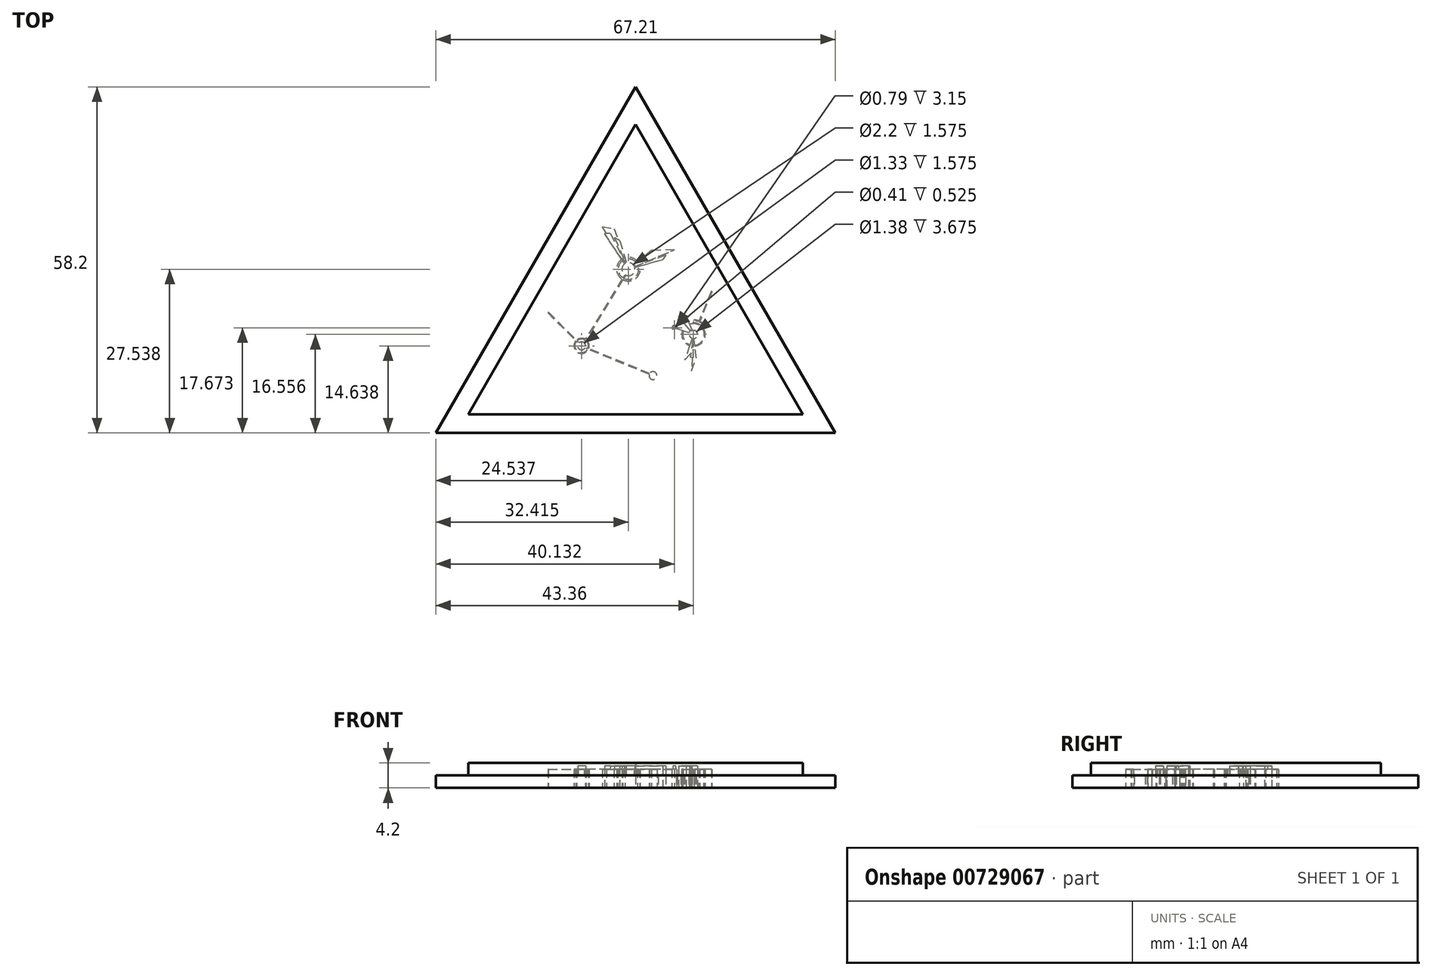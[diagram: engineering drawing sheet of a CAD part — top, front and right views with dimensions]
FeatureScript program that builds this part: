
annotation { "Feature Type Name" : "Feature", "Feature Type Description" : "" }
export const myFeature = defineFeature(function(context is Context, id is Id, definition is map)
    precondition{}
    {
        {
            var Q0;
            Q0=qCreatedBy(makeId("Top.planeOp"),FACE);
            var sketch = newSketch(context, id + "F0", { "sketchPlane" : qUnion([Q0])});
            skLineSegment(sketch, "E0", {"start": v(-5.3, -0.9) * mm, "end": v(-32.1, 45.54) * mm});
            skLineSegment(sketch, "E1", {"start": v(-58.9, -0.9) * mm, "end": v(-5.3, -0.9) * mm});
            skLineSegment(sketch, "E2", {"start": v(-58.9, -0.9) * mm, "end": v(-32.1, 45.54) * mm});
            skLineSegment(sketch, "E3", {"start": v(-32.03, 39.79) * mm, "end": v(-53.9, 1.92) * mm});
            skLineSegment(sketch, "E4", {"start": v(-53.9, 1.92) * mm, "end": v(-10.17, 1.92) * mm});
            skLineSegment(sketch, "E5", {"start": v(-10.17, 1.92) * mm, "end": v(-32.03, 39.79) * mm});
            skLineSegment(sketch, "E6.0", {"start": v(-0.1, -3.9) * mm, "end": v(-32.1, 51.54) * mm});
            skLineSegment(sketch, "E6.1", {"start": v(-64.1, -3.9) * mm, "end": v(-0.1, -3.9) * mm});
            skLineSegment(sketch, "E6.2", {"start": v(-64.1, -3.9) * mm, "end": v(-32.1, 51.54) * mm});
            skSolve(sketch);
        }
        {
            var Q0;
            Q0=makeQuery(id+"F0.imprint","IMPRINT",FACE,{"disambiguationData":[TD([[makeQuery(id+"F0.imprint","IMPRINT",EDGE,{"derivedFrom":sQuery(id+"F0.wireOp",EDGE,"E0")}),1.0]])]});
            extrude(context, id + "F1", {"entities" : qUnion([Q0]), "depth" : 4 * mm, "offsetDistance" : 25.4 * mm});
        }
        {
            var Q0;
            Q0=makeQuery(id+"F0.imprint","IMPRINT",FACE,{"disambiguationData":[TD([[makeQuery(id+"F0.imprint","IMPRINT",EDGE,{"derivedFrom":sQuery(id+"F0.wireOp",EDGE,"E3")}),1.0]])]});
            extrude(context, id + "F2", {"entities" : qUnion([Q0]), "operationType" : NewBodyOperationType.ADD, "depth" : 4 * mm, "offsetDistance" : 25.4 * mm});
        }
        {
            var Q0;
            Q0=qCreatedBy(makeId("Top.planeOp"),FACE);
            var sketch = newSketch(context, id + "F3", { "sketchPlane" : qUnion([Q0])});
            skCircle(sketch, "E7", {"center": v(-40.74, 10.05) * mm, "radius": 0.64 * mm});
            skArc(sketch, "E8", {"start": v(-29.9, 5.49) * mm, "mid": v(-28.73, 5.03) * mm, "end": v(-29.84, 5.63) * mm});
            skCircle(sketch, "E9", {"center": v(-33.24, 22.34) * mm, "radius": 1.05 * mm});
            skArc(sketch, "E10", {"start": v(-34.15, 23.7) * mm, "mid": v(-34.88, 22.31) * mm, "end": v(-34.12, 20.95) * mm});
            skArc(sketch, "E11", {"start": v(-34.3, 23.91) * mm, "mid": v(-35.13, 22.3) * mm, "end": v(-34.25, 20.73) * mm});
            skLineSegment(sketch, "E12", {"start": v(-33.9, 23.31) * mm, "end": v(-37.06, 28.04) * mm});
            skLineSegment(sketch, "E13", {"start": v(-36.14, 28.06) * mm, "end": v(-33.77, 23.39) * mm});
            skLineSegment(sketch, "E14", {"start": v(-36.14, 28.06) * mm, "end": v(-37.06, 28.04) * mm});
            skLineSegment(sketch, "E15", {"start": v(-35.47, 27.4) * mm, "end": v(-33.71, 23.41) * mm});
            skLineSegment(sketch, "E16", {"start": v(-34.67, 26.92) * mm, "end": v(-33.59, 23.46) * mm});
            skLineSegment(sketch, "E17", {"start": v(-34.67, 26.92) * mm, "end": v(-35.47, 27.4) * mm});
            skLineSegment(sketch, "E18.MirrorCS", {"start": v(-25.88, 25.44) * mm, "end": v(-29.56, 25.33) * mm});
            skLineSegment(sketch, "E19.MirrorCS", {"start": v(-32.15, 22.8) * mm, "end": v(-25.88, 25.44) * mm});
            skLineSegment(sketch, "E20.MirrorCS", {"start": v(-29.56, 25.33) * mm, "end": v(-32.33, 23.08) * mm});
            skLineSegment(sketch, "E21.MirrorCS", {"start": v(-27.26, 24.6) * mm, "end": v(-27.74, 23.9) * mm});
            skLineSegment(sketch, "E22.MirrorCS", {"start": v(-27.26, 24.6) * mm, "end": v(-32.14, 22.75) * mm});
            skLineSegment(sketch, "E23.MirrorCS", {"start": v(-32.1, 22.66) * mm, "end": v(-27.74, 23.9) * mm});
            skLineSegment(sketch, "E24.MirrorCS", {"start": v(-35.57, 28.84) * mm, "end": v(-34.94, 27.08) * mm});
            skLineSegment(sketch, "E25.MirrorCS", {"start": v(-34.63, 25.48) * mm, "end": v(-33.71, 23.41) * mm});
            skLineSegment(sketch, "E26.MirrorCS", {"start": v(-37.44, 29.13) * mm, "end": v(-35.57, 28.84) * mm});
            skLineSegment(sketch, "E27.MirrorCS", {"start": v(-34.15, 23.7) * mm, "end": v(-37.06, 28.04) * mm});
            skArc(sketch, "E28", {"start": v(-32.15, 22.8) * mm, "mid": v(-32.23, 22.94) * mm, "end": v(-32.33, 23.08) * mm});
            skLineSegment(sketch, "E29.trimOffspring", {"start": v(-36.77, 28.04) * mm, "end": v(-37.44, 29.13) * mm});
            skArc(sketch, "E30.trimOffspring", {"start": v(-33.77, 23.39) * mm, "mid": v(-33.83, 23.35) * mm, "end": v(-33.9, 23.31) * mm});
            skArc(sketch, "E31.trimOffspring", {"start": v(-33.59, 23.46) * mm, "mid": v(-33.65, 23.44) * mm, "end": v(-33.71, 23.41) * mm});
            skArc(sketch, "E32.trimOffspring", {"start": v(-32.1, 22.66) * mm, "mid": v(-32.12, 22.7) * mm, "end": v(-32.14, 22.75) * mm});
            skArc(sketch, "E33.trimOffspring", {"start": v(-31.96, 23.37) * mm, "mid": v(-32.76, 23.9) * mm, "end": v(-33.73, 23.9) * mm});
            skArc(sketch, "E34.trimOffspring", {"start": v(-31.77, 23.53) * mm, "mid": v(-32.69, 24.15) * mm, "end": v(-33.8, 24.15) * mm});
            skLineSegment(sketch, "E35.bottom", {"start": v(-29.9, 5.49) * mm, "end": v(-39.96, 9.6) * mm});
            skLineSegment(sketch, "E35.top", {"start": v(-29.84, 5.63) * mm, "end": v(-39.9, 9.74) * mm});
            skLineSegment(sketch, "E35.right", {"start": v(-39.96, 9.6) * mm, "end": v(-39.9, 9.74) * mm});
            skArc(sketch, "E36", {"start": v(-40.2, 11) * mm, "mid": v(-40.86, 11.14) * mm, "end": v(-41.47, 10.87) * mm});
            skArc(sketch, "E37", {"start": v(-40.14, 11.11) * mm, "mid": v(-40.87, 11.26) * mm, "end": v(-41.56, 10.96) * mm});
            skLineSegment(sketch, "E38.top", {"start": v(-41.3, 10.71) * mm, "end": v(-41.4, 10.62) * mm});
            skLineSegment(sketch, "E38.left", {"start": v(-46.07, 15.46) * mm, "end": v(-41.3, 10.71) * mm});
            skLineSegment(sketch, "E38.right", {"start": v(-46.14, 15.35) * mm, "end": v(-41.4, 10.62) * mm});
            skCircle(sketch, "E39", {"center": v(-22.81, 11.88) * mm, "radius": 0.66 * mm});
            skArc(sketch, "E40", {"start": v(-24.59, 12.5) * mm, "mid": v(-24.5, 11.06) * mm, "end": v(-23.43, 10.1) * mm});
            skArc(sketch, "E41", {"start": v(-24.45, 12.44) * mm, "mid": v(-24.37, 11.12) * mm, "end": v(-23.38, 10.24) * mm});
            skLineSegment(sketch, "E42", {"start": v(-22.81, 8.13) * mm, "end": v(-22.81, 11.08) * mm});
            skLineSegment(sketch, "E43", {"start": v(-22.81, 8.13) * mm, "end": v(-23.33, 8.2) * mm});
            skLineSegment(sketch, "E44", {"start": v(-23.16, 6.02) * mm, "end": v(-22.38, 8.1) * mm});
            skLineSegment(sketch, "E45", {"start": v(-22.38, 8.1) * mm, "end": v(-22.72, 11.09) * mm});
            skLineSegment(sketch, "E46", {"start": v(-24.23, 7.77) * mm, "end": v(-23.24, 8.83) * mm});
            skCircle(sketch, "E47", {"center": v(-25.89, 12.94) * mm, "radius": 0.38 * mm});
            skLineSegment(sketch, "E48", {"start": v(-25.2, 14.7) * mm, "end": v(-24.02, 14.94) * mm});
            skLineSegment(sketch, "E49", {"start": v(-24.02, 14.94) * mm, "end": v(-23.1, 12.62) * mm});
            skArc(sketch, "E50", {"start": v(-25.42, 12.78) * mm, "mid": v(-25.42, 13.08) * mm, "end": v(-25.58, 13.32) * mm});
            skLineSegment(sketch, "E51.trimOffspring", {"start": v(-25.58, 13.32) * mm, "end": v(-24.82, 14.25) * mm});
            skCircle(sketch, "E52", {"center": v(-25.89, 12.94) * mm, "radius": 0.2 * mm});
            skArc(sketch, "E53", {"start": v(-23.07, 11.13) * mm, "mid": v(-22.9, 11.09) * mm, "end": v(-22.72, 11.09) * mm});
            skLineSegment(sketch, "E54.trimOffspring", {"start": v(-23.33, 12.49) * mm, "end": v(-25.2, 14.7) * mm});
            skLineSegment(sketch, "E55.trimOffspring", {"start": v(-23.57, 12.14) * mm, "end": v(-25.42, 12.78) * mm});
            skLineSegment(sketch, "E56.trimOffspring", {"start": v(-23.07, 11.13) * mm, "end": v(-24.23, 7.77) * mm});
            skLineSegment(sketch, "E57.trimOffspring", {"start": v(-22.92, 11.09) * mm, "end": v(-23.33, 8.2) * mm});
            skLineSegment(sketch, "E58.trimOffspring", {"start": v(-23.03, 8.16) * mm, "end": v(-23.16, 6.02) * mm});
            skArc(sketch, "E59.trimOffspring", {"start": v(-22.62, 10.16) * mm, "mid": v(-21.14, 12.3) * mm, "end": v(-23.45, 13.49) * mm});
            skArc(sketch, "E60.trimOffspring", {"start": v(-22.6, 10.01) * mm, "mid": v(-21, 12.33) * mm, "end": v(-23.5, 13.62) * mm});
            skArc(sketch, "E61.trimOffspring", {"start": v(-23.1, 12.62) * mm, "mid": v(-23.39, 12.43) * mm, "end": v(-23.57, 12.14) * mm});
            skLineSegment(sketch, "E62.left", {"start": v(-19.86, 18.7) * mm, "end": v(-21.8, 13.99) * mm});
            skLineSegment(sketch, "E62.right", {"start": v(-19.94, 18.84) * mm, "end": v(-21.92, 14.04) * mm});
            skArc(sketch, "E63", {"start": v(-21.1, 13.47) * mm, "mid": v(-21.43, 13.76) * mm, "end": v(-21.8, 13.99) * mm});
            skArc(sketch, "E64", {"start": v(-21.2, 13.38) * mm, "mid": v(-21.9, 13.89) * mm, "end": v(-22.75, 14.09) * mm});
            skLineSegment(sketch, "E65.trimOffspring", {"start": v(-21.2, 13.38) * mm, "end": v(-21.1, 13.47) * mm});
            skLineSegment(sketch, "E66.trimOffspring", {"start": v(-22.75, 14.09) * mm, "end": v(-22.74, 14.21) * mm});
            skLineSegment(sketch, "E67.bottom", {"start": v(-33.87, 21.35) * mm, "end": v(-33.76, 21.29) * mm});
            skLineSegment(sketch, "E67.top", {"start": v(-40.33, 10.81) * mm, "end": v(-40.22, 10.75) * mm});
            skLineSegment(sketch, "E67.left", {"start": v(-33.87, 21.35) * mm, "end": v(-40.33, 10.81) * mm});
            skLineSegment(sketch, "E67.right", {"start": v(-33.76, 21.29) * mm, "end": v(-40.22, 10.75) * mm});
            skArc(sketch, "E68.trimOffspring", {"start": v(-34, 20.88) * mm, "mid": v(-32.2, 21.06) * mm, "end": v(-31.66, 22.78) * mm});
            skArc(sketch, "E69.trimOffspring", {"start": v(-34.14, 20.67) * mm, "mid": v(-32.05, 20.86) * mm, "end": v(-31.41, 22.85) * mm});
            skArc(sketch, "E70.trimOffspring", {"start": v(-41.56, 10.78) * mm, "mid": v(-41.37, 9.16) * mm, "end": v(-39.79, 9.52) * mm});
            skArc(sketch, "E71.trimOffspring", {"start": v(-41.65, 10.87) * mm, "mid": v(-41.44, 9.06) * mm, "end": v(-39.67, 9.47) * mm});
            skArc(sketch, "E72.trimOffspring", {"start": v(-39.72, 9.67) * mm, "mid": v(-39.7, 10.37) * mm, "end": v(-40.1, 10.94) * mm});
            skArc(sketch, "E73.trimOffspring", {"start": v(-39.6, 9.62) * mm, "mid": v(-39.58, 10.4) * mm, "end": v(-40.04, 11.04) * mm});
            skArc(sketch, "E74.trimOffspring", {"start": v(-21.92, 14.04) * mm, "mid": v(-22.33, 14.16) * mm, "end": v(-22.74, 14.21) * mm});
            skLineSegment(sketch, "E75", {"start": v(-33.9, 23.63) * mm, "end": v(-33.83, 23.67) * mm});
            skLineSegment(sketch, "E76", {"start": v(-19.94, 18.84) * mm, "end": v(-19.86, 18.7) * mm});
            skLineSegment(sketch, "E77", {"start": v(-27.26, 24.6) * mm, "end": v(-28.47, 24.35) * mm});
            skLineSegment(sketch, "E78", {"start": v(-46.07, 15.46) * mm, "end": v(-46.14, 15.35) * mm});
            skSolve(sketch);
        }
        {
            var Q0;
            {var subQ1=sQuery(id+"F3.wireOp",EDGE,"E18.MirrorCS");Q0=makeQuery(id+"F3.imprint","IMPRINT",FACE,{"disambiguationData":[TD([[makeQuery(id+"F3.imprint","IMPRINT",EDGE,{"derivedFrom":subQ1}),1.0]])]});}
            var Q1;
            {var subQ0=sQuery(id+"F3.wireOp",EDGE,"E68.trimOffspring");Q1=makeQuery(id+"F3.imprint","IMPRINT",FACE,{"disambiguationData":[TD([[makeQuery(id+"F3.imprint","IMPRINT",EDGE,{"derivedFrom":subQ0}),-1.0]])]});}
            var Q2;
            {var subQ0=sQuery(id+"F3.wireOp",EDGE,"E10");Q2=makeQuery(id+"F3.imprint","IMPRINT",FACE,{"disambiguationData":[TD([[makeQuery(id+"F3.imprint","IMPRINT",EDGE,{"derivedFrom":subQ0}),-1.0]])]});}
            var Q3;
            {var subQ0=sQuery(id+"F3.wireOp",EDGE,"E33.trimOffspring");Q3=makeQuery(id+"F3.imprint","IMPRINT",FACE,{"disambiguationData":[TD([[makeQuery(id+"F3.imprint","IMPRINT",EDGE,{"derivedFrom":subQ0}),-1.0]])]});}
            var Q4;
            {var subQ6=sQuery(id+"F3.wireOp",EDGE,"E15");Q4=makeQuery(id+"F3.imprint","IMPRINT",FACE,{"disambiguationData":[TD([[makeQuery(id+"F3.imprint","IMPRINT",EDGE,{"derivedFrom":subQ6}),-1.0]])]});}
            var Q5;
            {var subQ4=sQuery(id+"F3.wireOp",EDGE,"E67.bottom");Q5=makeQuery(id+"F3.imprint","IMPRINT",FACE,{"disambiguationData":[TD([[makeQuery(id+"F3.imprint","IMPRINT",EDGE,{"derivedFrom":subQ4}),-1.0]])]});}
            var Q6;
            Q6=makeQuery(id+"F3.imprint","IMPRINT",FACE,{"disambiguationData":[TD([[makeQuery(id+"F3.imprint","IMPRINT",EDGE,{"derivedFrom":sQuery(id+"F3.wireOp",EDGE,"E62.left")}),-1.0]])]});
            var Q7;
            {var subQ0=sQuery(id+"F3.wireOp",EDGE,"E59.trimOffspring");Q7=makeQuery(id+"F3.imprint","IMPRINT",FACE,{"disambiguationData":[TD([[makeQuery(id+"F3.imprint","IMPRINT",EDGE,{"derivedFrom":subQ0}),-1.0]])]});}
            var Q8;
            {var subQ0=sQuery(id+"F3.wireOp",EDGE,"E40");Q8=makeQuery(id+"F3.imprint","IMPRINT",FACE,{"disambiguationData":[TD([[makeQuery(id+"F3.imprint","IMPRINT",EDGE,{"derivedFrom":subQ0}),1.0]])]});}
            var Q9;
            {var subQ1=sQuery(id+"F3.wireOp",EDGE,"E42");Q9=makeQuery(id+"F3.imprint","IMPRINT",FACE,{"disambiguationData":[TD([[makeQuery(id+"F3.imprint","IMPRINT",EDGE,{"derivedFrom":subQ1}),1.0]])]});}
            var Q10;
            Q10=makeQuery(id+"F3.imprint","IMPRINT",FACE,{"disambiguationData":[TD([[makeQuery(id+"F3.imprint","IMPRINT",EDGE,{"derivedFrom":sQuery(id+"F3.wireOp",EDGE,"E47")}),1.0]])]});
            var Q11;
            {var subQ0=sQuery(id+"F3.wireOp",EDGE,"E72.trimOffspring");Q11=makeQuery(id+"F3.imprint","IMPRINT",FACE,{"disambiguationData":[TD([[makeQuery(id+"F3.imprint","IMPRINT",EDGE,{"derivedFrom":subQ0}),-1.0]])]});}
            var Q12;
            {var subQ3=sQuery(id+"F3.wireOp",EDGE,"E8");Q12=makeQuery(id+"F3.imprint","IMPRINT",FACE,{"disambiguationData":[TD([[makeQuery(id+"F3.imprint","IMPRINT",EDGE,{"derivedFrom":subQ3}),1.0]])]});}
            var Q13;
            {var subQ2=sQuery(id+"F3.wireOp",EDGE,"E38.top");Q13=makeQuery(id+"F3.imprint","IMPRINT",FACE,{"disambiguationData":[TD([[makeQuery(id+"F3.imprint","IMPRINT",EDGE,{"derivedFrom":subQ2}),-1.0]])]});}
            var Q14;
            {var subQ0=sQuery(id+"F3.wireOp",EDGE,"E36");Q14=makeQuery(id+"F3.imprint","IMPRINT",FACE,{"disambiguationData":[TD([[makeQuery(id+"F3.imprint","IMPRINT",EDGE,{"derivedFrom":subQ0}),-1.0]])]});}
            var Q15;
            {var subQ0=sQuery(id+"F3.wireOp",EDGE,"E70.trimOffspring");Q15=makeQuery(id+"F3.imprint","IMPRINT",FACE,{"disambiguationData":[TD([[makeQuery(id+"F3.imprint","IMPRINT",EDGE,{"derivedFrom":subQ0}),-1.0]])]});}
            extrude(context, id + "F4", {"entities" : qUnion([Q0, Q1, Q2, Q3, Q4, Q5, Q6, Q7, Q8, Q9, Q10, Q11, Q12, Q13, Q14, Q15]), "operationType" : NewBodyOperationType.REMOVE, "depth" : 3 * mm, "offsetDistance" : 25 * mm});
        }
        {
            var Q0;
            {var subQ7=sQuery(id+"F3.wireOp",EDGE,"E46");Q0=makeQuery(id+"F3.imprint","IMPRINT",FACE,{"disambiguationData":[TD([[makeQuery(id+"F3.imprint","IMPRINT",EDGE,{"derivedFrom":subQ7}),1.0]])]});}
            var Q1;
            {var subQ4=sQuery(id+"F3.wireOp",EDGE,"E42");Q1=makeQuery(id+"F3.imprint","IMPRINT",FACE,{"disambiguationData":[TD([[makeQuery(id+"F3.imprint","IMPRINT",EDGE,{"derivedFrom":subQ4}),-1.0]])]});}
            var Q2;
            {var subQ7=sQuery(id+"F3.wireOp",EDGE,"E50");Q2=makeQuery(id+"F3.imprint","IMPRINT",FACE,{"disambiguationData":[TD([[makeQuery(id+"F3.imprint","IMPRINT",EDGE,{"derivedFrom":subQ7}),-1.0]])]});}
            var Q3;
            Q3=makeQuery(id+"F3.imprint","IMPRINT",FACE,{"disambiguationData":[TD([[makeQuery(id+"F3.imprint","IMPRINT",EDGE,{"derivedFrom":sQuery(id+"F3.wireOp",EDGE,"E7")}),-1.0]])]});
            var Q4;
            Q4=makeQuery(id+"F3.imprint","IMPRINT",FACE,{"disambiguationData":[TD([[makeQuery(id+"F3.imprint","IMPRINT",EDGE,{"derivedFrom":sQuery(id+"F3.wireOp",EDGE,"E9")}),-1.0]])]});
            extrude(context, id + "F5", {"entities" : qUnion([Q0, Q1, Q2, Q3, Q4]), "operationType" : NewBodyOperationType.REMOVE, "depth" : 2 * mm, "offsetDistance" : 25 * mm});
        }
        {
            var Q0;
            Q0=makeQuery(id+"F3.imprint","IMPRINT",FACE,{"disambiguationData":[TD([[makeQuery(id+"F3.imprint","IMPRINT",EDGE,{"derivedFrom":sQuery(id+"F3.wireOp",EDGE,"E52")}),1.0]])]});
            var Q1;
            Q1=makeQuery(id+"F3.imprint","IMPRINT",FACE,{"disambiguationData":[TD([[makeQuery(id+"F3.imprint","IMPRINT",EDGE,{"derivedFrom":sQuery(id+"F3.wireOp",EDGE,"E39")}),1.0]])]});
            var Q2;
            {var subQ5=sQuery(id+"F3.wireOp",EDGE,"E48");Q2=makeQuery(id+"F3.imprint","IMPRINT",FACE,{"disambiguationData":[TD([[makeQuery(id+"F3.imprint","IMPRINT",EDGE,{"derivedFrom":subQ5}),-1.0]])]});}
            var Q3;
            {var subQ6=sQuery(id+"F3.wireOp",EDGE,"E15");Q3=makeQuery(id+"F3.imprint","IMPRINT",FACE,{"disambiguationData":[TD([[makeQuery(id+"F3.imprint","IMPRINT",EDGE,{"derivedFrom":subQ6}),1.0]])]});}
            var Q4;
            {var subQ4=sQuery(id+"F3.wireOp",EDGE,"E21.MirrorCS");Q4=makeQuery(id+"F3.imprint","IMPRINT",FACE,{"disambiguationData":[TD([[makeQuery(id+"F3.imprint","IMPRINT",EDGE,{"derivedFrom":subQ4}),-1.0]])]});}
            var Q5;
            Q5=makeQuery(id+"F3.imprint","IMPRINT",FACE,{"disambiguationData":[TD([[makeQuery(id+"F3.imprint","IMPRINT",EDGE,{"derivedFrom":sQuery(id+"F3.wireOp",EDGE,"E9")}),1.0]])]});
            var Q6;
            {var subQ1=sQuery(id+"F3.wireOp",EDGE,"E12");Q6=makeQuery(id+"F3.imprint","IMPRINT",FACE,{"disambiguationData":[TD([[makeQuery(id+"F3.imprint","IMPRINT",EDGE,{"derivedFrom":subQ1}),-1.0]])]});}
            var Q7;
            Q7=makeQuery(id+"F3.imprint","IMPRINT",FACE,{"disambiguationData":[TD([[makeQuery(id+"F3.imprint","IMPRINT",EDGE,{"derivedFrom":sQuery(id+"F3.wireOp",EDGE,"E7")}),1.0]])]});
            extrude(context, id + "F6", {"entities" : qUnion([Q0, Q1, Q2, Q3, Q4, Q5, Q6, Q7]), "operationType" : NewBodyOperationType.REMOVE, "depth" : 3.5 * mm, "offsetDistance" : 25 * mm});
        }
        {
            var Q0;
            Q0=makeQuery(id+"F0.imprint","IMPRINT",FACE,{"disambiguationData":[TD([[makeQuery(id+"F0.imprint","IMPRINT",EDGE,{"derivedFrom":sQuery(id+"F0.wireOp",EDGE,"E0")}),-1.0]])]});
            extrude(context, id + "F7", {"entities" : qUnion([Q0]), "operationType" : NewBodyOperationType.ADD, "depth" : 2 * mm, "offsetDistance" : 25 * mm});
        }
        {
            var Q0;
            Q0=makeQuery(id+"F1.opExtrude","SWEPT_BODY",BODY,{"disambiguationData":[OSD([sQuery(id+"F0.wireOp",EDGE,"E0"),sQuery(id+"F0.wireOp",EDGE,"E1"),sQuery(id+"F0.wireOp",EDGE,"E2"),sQuery(id+"F0.wireOp",EDGE,"E3"),sQuery(id+"F0.wireOp",EDGE,"E4"),sQuery(id+"F0.wireOp",EDGE,"E5")])]});
            var Q1;
            Q1=sQuery(id+"F0.wireOp",VERTEX,"E6.2.start");
            transform(context, id + "F8", {"entities" : qUnion([Q0]), "transformType" : TransformType.SCALE_UNIFORMLY, "scale" : 1.05, "scalePoint" : qUnion([Q1]), "makeCopy" : false});
        }
    });
